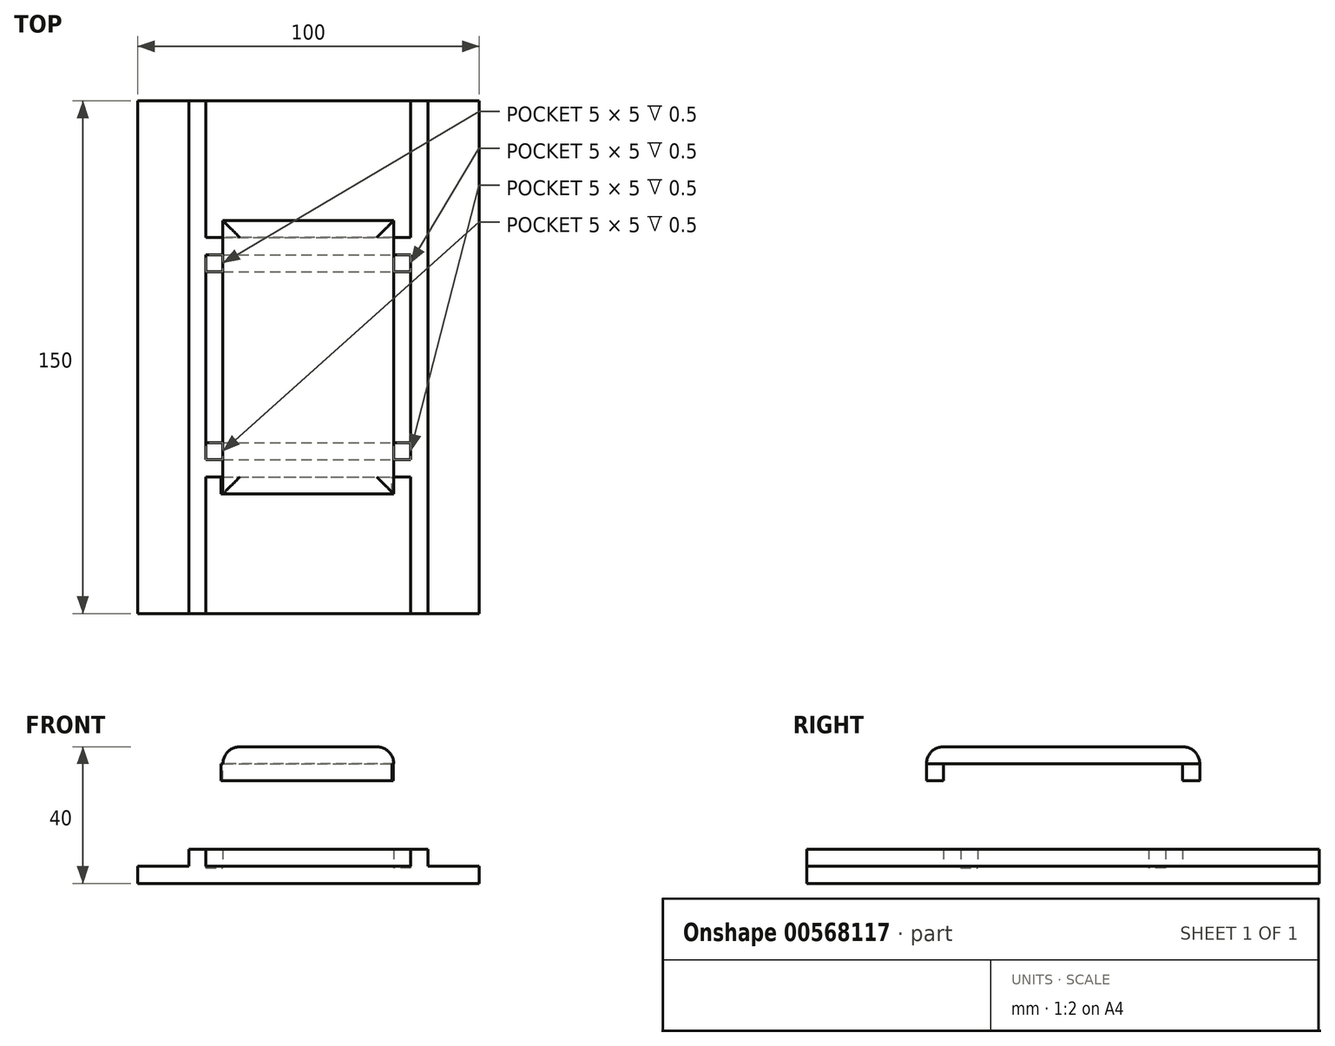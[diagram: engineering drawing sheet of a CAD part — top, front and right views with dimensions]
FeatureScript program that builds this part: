
annotation { "Feature Type Name" : "Feature", "Feature Type Description" : "" }
export const myFeature = defineFeature(function(context is Context, id is Id, definition is map)
    precondition{}
    {
        {
            var Q0;
            Q0=qCreatedBy(makeId("Top.planeOp"),FACE);
            var sketch = newSketch(context, id + "F0", { "sketchPlane" : qUnion([Q0])});
            skLineSegment(sketch, "E0.bottom", {"start": v(0, 150) * mm, "end": v(100, 150) * mm});
            skLineSegment(sketch, "E0.top", {"start": v(0, 0) * mm, "end": v(100, 0) * mm});
            skLineSegment(sketch, "E0.left", {"start": v(0, 150) * mm, "end": v(0, 0) * mm});
            skLineSegment(sketch, "E0.right", {"start": v(100, 150) * mm, "end": v(100, 0) * mm});
            skSolve(sketch);
        }
        {
            var Q0;
            Q0 = qSketchRegion(id + "F0", true);
            extrude(context, id + "F1", {"entities" : qUnion([Q0]), "depth" : 5 * mm, "offsetDistance" : 25 * mm});
        }
        {
            var Q0;
            Q0=makeQuery(id+"F1.opExtrude","CAP_FACE",FACE,{"disambiguationData":[OSD([sQuery(id+"F0.wireOp",EDGE,"E0.bottom"),sQuery(id+"F0.wireOp",EDGE,"E0.top"),sQuery(id+"F0.wireOp",EDGE,"E0.left"),sQuery(id+"F0.wireOp",EDGE,"E0.right")])],"isStart":false});
            cPlane(context, id + "F2", {"entities" : qUnion([Q0]), "cplaneType" : CPlaneType.OFFSET, "offset" : 0 * mm, "width" : 150 * mm, "height" : 150 * mm});
        }
        {
            var Q0;
            Q0=qCreatedBy(id+"F2.planeOp",FACE);
            var sketch = newSketch(context, id + "F3", { "sketchPlane" : qUnion([Q0])});
            skLineSegment(sketch, "E1.bottom", {"start": v(15, 150) * mm, "end": v(20, 150) * mm});
            skLineSegment(sketch, "E1.top", {"start": v(15, 0) * mm, "end": v(20, 0) * mm});
            skLineSegment(sketch, "E1.left", {"start": v(15, 150) * mm, "end": v(15, 0) * mm});
            skLineSegment(sketch, "E1.right", {"start": v(20, 150) * mm, "end": v(20, 0) * mm});
            skLineSegment(sketch, "E2.bottom", {"start": v(80, 0) * mm, "end": v(85, 0) * mm});
            skLineSegment(sketch, "E2.top", {"start": v(80, 150) * mm, "end": v(85, 150) * mm});
            skLineSegment(sketch, "E2.left", {"start": v(80, 0) * mm, "end": v(80, 150) * mm});
            skLineSegment(sketch, "E2.right", {"start": v(85, 0) * mm, "end": v(85, 150) * mm});
            skLineSegment(sketch, "E3.bottom", {"start": v(20, 105) * mm, "end": v(80, 105) * mm});
            skLineSegment(sketch, "E3.top", {"start": v(20, 110) * mm, "end": v(80, 110) * mm});
            skLineSegment(sketch, "E3.left", {"start": v(20, 105) * mm, "end": v(20, 110) * mm});
            skLineSegment(sketch, "E3.right", {"start": v(80, 105) * mm, "end": v(80, 110) * mm});
            skLineSegment(sketch, "E4.bottom", {"start": v(20, 45) * mm, "end": v(80, 45) * mm});
            skLineSegment(sketch, "E4.top", {"start": v(20, 40) * mm, "end": v(80, 40) * mm});
            skLineSegment(sketch, "E4.left", {"start": v(20, 45) * mm, "end": v(20, 40) * mm});
            skLineSegment(sketch, "E4.right", {"start": v(80, 45) * mm, "end": v(80, 40) * mm});
            skSolve(sketch);
        }
        {
            var Q0;
            Q0 = qSketchRegion(id + "F3", true);
            extrude(context, id + "F4", {"entities" : qUnion([Q0]), "operationType" : NewBodyOperationType.ADD, "depth" : 5 * mm, "offsetDistance" : 25 * mm});
        }
        {
            var Q0;
            Q0=qCreatedBy(id+"F2.planeOp",FACE);
            var sketch = newSketch(context, id + "F5", { "sketchPlane" : qUnion([Q0])});
            skLineSegment(sketch, "E5.bottom", {"start": v(20, 105) * mm, "end": v(25, 105) * mm});
            skLineSegment(sketch, "E5.top", {"start": v(20, 100) * mm, "end": v(25, 100) * mm});
            skLineSegment(sketch, "E5.left", {"start": v(20, 105) * mm, "end": v(20, 100) * mm});
            skLineSegment(sketch, "E5.right", {"start": v(25, 105) * mm, "end": v(25, 100) * mm});
            skLineSegment(sketch, "E6.bottom", {"start": v(80, 105) * mm, "end": v(75, 105) * mm});
            skLineSegment(sketch, "E6.top", {"start": v(80, 100) * mm, "end": v(75, 100) * mm});
            skLineSegment(sketch, "E6.left", {"start": v(80, 105) * mm, "end": v(80, 100) * mm});
            skLineSegment(sketch, "E6.right", {"start": v(75, 105) * mm, "end": v(75, 100) * mm});
            skLineSegment(sketch, "E7.bottom", {"start": v(80, 45) * mm, "end": v(75, 45) * mm});
            skLineSegment(sketch, "E7.top", {"start": v(80, 50) * mm, "end": v(75, 50) * mm});
            skLineSegment(sketch, "E7.left", {"start": v(80, 45) * mm, "end": v(80, 50) * mm});
            skLineSegment(sketch, "E7.right", {"start": v(75, 45) * mm, "end": v(75, 50) * mm});
            skLineSegment(sketch, "E8.bottom", {"start": v(20, 45) * mm, "end": v(25, 45) * mm});
            skLineSegment(sketch, "E8.top", {"start": v(20, 50) * mm, "end": v(25, 50) * mm});
            skLineSegment(sketch, "E8.left", {"start": v(20, 45) * mm, "end": v(20, 50) * mm});
            skLineSegment(sketch, "E8.right", {"start": v(25, 45) * mm, "end": v(25, 50) * mm});
            skSolve(sketch);
        }
        {
            var Q0;
            Q0 = qSketchRegion(id + "F5", true);
            extrude(context, id + "F6", {"entities" : qUnion([Q0]), "operationType" : NewBodyOperationType.REMOVE, "oppositeDirection" : true, "depth" : 0.5 * mm, "offsetDistance" : 25 * mm});
        }
        {
            var Q0;
            Q0=qCreatedBy(id+"F2.planeOp",FACE);
            var sketch = newSketch(context, id + "F7", { "sketchPlane" : qUnion([Q0])});
            skLineSegment(sketch, "E9.bottom", {"start": v(25, 100) * mm, "end": v(75, 100) * mm});
            skLineSegment(sketch, "E9.top", {"start": v(25, 50) * mm, "end": v(75, 50) * mm});
            skLineSegment(sketch, "E9.left", {"start": v(25, 100) * mm, "end": v(25, 50) * mm});
            skLineSegment(sketch, "E9.right", {"start": v(75, 100) * mm, "end": v(75, 50) * mm});
            skSolve(sketch);
        }
        {
            var Q0;
            Q0 = qSketchRegion(id + "F7", true);
            extrude(context, id + "F8", {"entities" : qUnion([Q0]), "operationType" : NewBodyOperationType.ADD, "depth" : 5 * mm, "offsetDistance" : 25 * mm});
        }
        {
            var Q0;
            Q0=makeQuery(id+"F8.opExtrude","CAP_FACE",FACE,{"disambiguationData":[OSD([sQuery(id+"F7.wireOp",EDGE,"E9.bottom"),sQuery(id+"F7.wireOp",EDGE,"E9.top"),sQuery(id+"F7.wireOp",EDGE,"E9.left"),sQuery(id+"F7.wireOp",EDGE,"E9.right")])],"isStart":false});
            cPlane(context, id + "F9", {"entities" : qUnion([Q0]), "cplaneType" : CPlaneType.OFFSET, "offset" : 25 * mm, "width" : 150 * mm, "height" : 150 * mm});
        }
        {
            var Q0;
            Q0=qCreatedBy(id+"F9.planeOp",FACE);
            var sketch = newSketch(context, id + "F10", { "sketchPlane" : qUnion([Q0])});
            skLineSegment(sketch, "E10.bottom", {"start": v(25, 115) * mm, "end": v(75, 115) * mm});
            skLineSegment(sketch, "E10.top", {"start": v(25, 35) * mm, "end": v(75, 35) * mm});
            skLineSegment(sketch, "E10.left", {"start": v(25, 115) * mm, "end": v(25, 35) * mm});
            skLineSegment(sketch, "E10.right", {"start": v(75, 115) * mm, "end": v(75, 35) * mm});
            skLineSegment(sketch, "E11", {"start": v(25, 40) * mm, "end": v(75, 40) * mm});
            skLineSegment(sketch, "E12", {"start": v(75, 110) * mm, "end": v(25, 110) * mm});
            skSolve(sketch);
        }
        {
            var Q0;
            Q0 = qSketchRegion(id + "F10", true);
            extrude(context, id + "F11", {"entities" : qUnion([Q0]), "depth" : 5 * mm, "offsetDistance" : 25 * mm});
        }
        {
            var Q0;
            Q0=makeQuery(id+"F11.opExtrude","CAP_FACE",FACE,{"disambiguationData":[OSD([sQuery(id+"F10.wireOp",EDGE,"E10.bottom"),sQuery(id+"F10.wireOp",EDGE,"E10.top"),sQuery(id+"F10.wireOp",EDGE,"E10.left"),sQuery(id+"F10.wireOp",EDGE,"E10.right")])],"isStart":true});
            cPlane(context, id + "F12", {"entities" : qUnion([Q0]), "cplaneType" : CPlaneType.OFFSET, "offset" : 0 * mm, "width" : 150 * mm, "height" : 150 * mm});
        }
        {
            var Q0;
            Q0=qCreatedBy(id+"F12.planeOp",FACE);
            var sketch = newSketch(context, id + "F13", { "sketchPlane" : qUnion([Q0])});
            skLineSegment(sketch, "E13.bottom", {"start": v(24.43, -35) * mm, "end": v(74.43, -35) * mm});
            skLineSegment(sketch, "E13.top", {"start": v(24.43, -40) * mm, "end": v(74.43, -40) * mm});
            skLineSegment(sketch, "E13.left", {"start": v(24.43, -35) * mm, "end": v(24.43, -40) * mm});
            skLineSegment(sketch, "E13.right", {"start": v(74.43, -35) * mm, "end": v(74.43, -40) * mm});
            skLineSegment(sketch, "E14.bottom", {"start": v(74.9, -115) * mm, "end": v(24.9, -115) * mm});
            skLineSegment(sketch, "E14.top", {"start": v(74.9, -110) * mm, "end": v(24.9, -110) * mm});
            skLineSegment(sketch, "E14.left", {"start": v(74.9, -115) * mm, "end": v(74.9, -110) * mm});
            skLineSegment(sketch, "E14.right", {"start": v(24.9, -115) * mm, "end": v(24.9, -110) * mm});
            skSolve(sketch);
        }
        {
            var Q0;
            Q0 = qSketchRegion(id + "F13", true);
            extrude(context, id + "F14", {"entities" : qUnion([Q0]), "operationType" : NewBodyOperationType.ADD, "depth" : 5 * mm, "offsetDistance" : 25 * mm});
        }
        {
            var Q0;
            Q0=makeQuery(id+"F11.opExtrude","CAP_FACE",FACE,{"disambiguationData":[OSD([sQuery(id+"F10.wireOp",EDGE,"E10.bottom"),sQuery(id+"F10.wireOp",EDGE,"E10.top"),sQuery(id+"F10.wireOp",EDGE,"E10.left"),sQuery(id+"F10.wireOp",EDGE,"E10.right")])],"isStart":false});
            fillet(context, id + "F15", {"entities" : qUnion([Q0]), "radius" : 5 * mm, "tangentPropagation" : true, "allowEdgeOverflow" : false});
        }
    });
